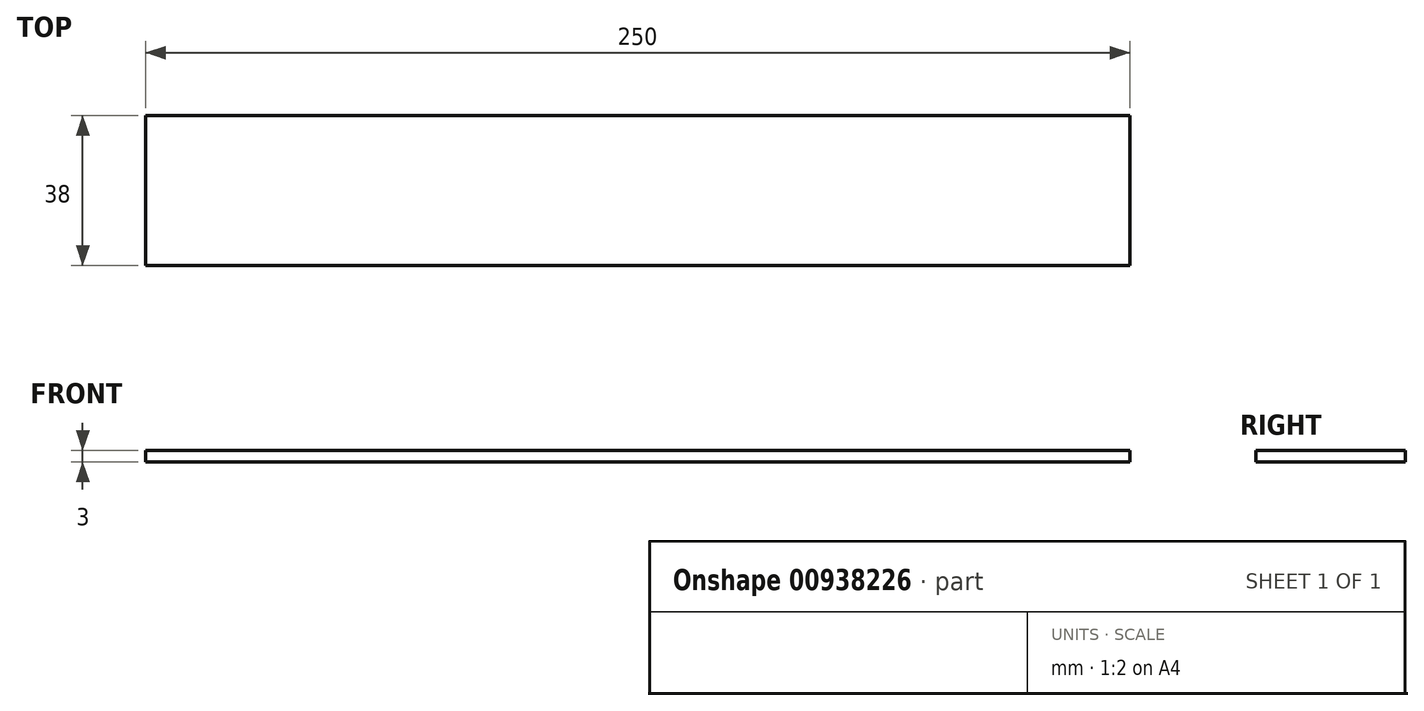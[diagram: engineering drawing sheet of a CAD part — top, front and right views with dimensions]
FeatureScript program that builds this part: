
annotation { "Feature Type Name" : "Feature", "Feature Type Description" : "" }
export const myFeature = defineFeature(function(context is Context, id is Id, definition is map)
    precondition{}
    {
        {
            var Q0;
            Q0=qCreatedBy(makeId("Top.planeOp"),FACE);
            var sketch = newSketch(context, id + "F0", { "sketchPlane" : qUnion([Q0])});
            skLineSegment(sketch, "E0.bottom", {"start": v(0, 0) * mm, "end": v(250, 0) * mm});
            skLineSegment(sketch, "E0.top", {"start": v(0, 38) * mm, "end": v(250, 38) * mm});
            skLineSegment(sketch, "E0.left", {"start": v(0, 0) * mm, "end": v(0, 38) * mm});
            skLineSegment(sketch, "E0.right", {"start": v(250, 0) * mm, "end": v(250, 38) * mm});
            skSolve(sketch);
        }
        {
            var Q0;
            Q0=makeQuery(id+"F0.imprint","IMPRINT",FACE,{"disambiguationData":[TD([[makeQuery(id+"F0.imprint","IMPRINT",EDGE,{"derivedFrom":sQuery(id+"F0.wireOp",EDGE,"E0.bottom")}),1.0]])]});
            extrude(context, id + "F1", {"entities" : qUnion([Q0]), "depth" : 3 * mm, "offsetDistance" : 25 * mm});
        }
    });
